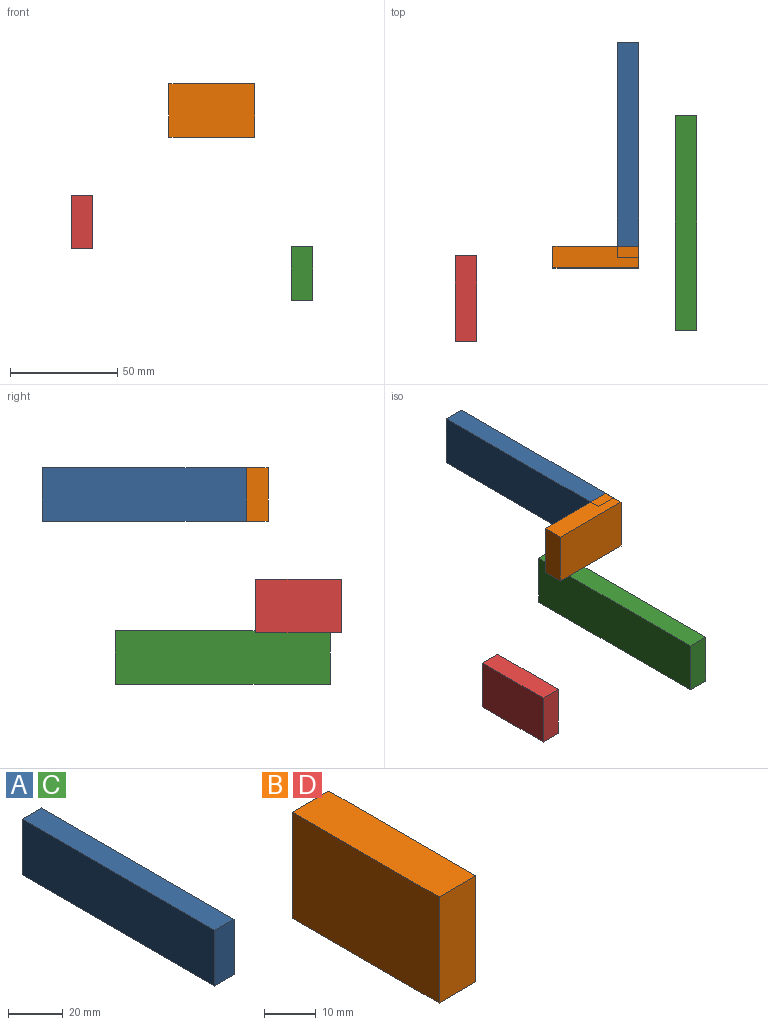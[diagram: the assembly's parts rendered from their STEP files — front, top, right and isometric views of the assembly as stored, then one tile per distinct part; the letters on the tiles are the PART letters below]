
ASSEMBLY  parts=4 mates=1
PART A: 6 faces, bbox 10x100x25 mm
  f0: plane 100x10mm, normal (0,0,1), area 1000mm2, adj f1,f3,f4,f5
  f1: plane 100x25mm, normal (-1,0,0), area 2500mm2, adj f0,f2,f4,f5
  f2: plane 100x10mm, normal (0,0,-1), area 1000mm2, adj f1,f3,f4,f5
  f3: plane 100x25mm, normal (1,0,0), area 2500mm2, adj f0,f2,f4,f5
  f4: plane 25x10mm, normal (0,-1,0), area 250mm2, adj f0,f1,f2,f3
  f5: plane 25x10mm, normal (0,1,0), area 250mm2, adj f0,f1,f2,f3
PART B: 6 faces, bbox 10x40x25 mm
  f0: plane 40x10mm, normal (0,0,1), area 400mm2, adj f1,f3,f4,f5
  f1: plane 40x25mm, normal (-1,0,0), area 1000mm2, adj f0,f2,f4,f5
  f2: plane 40x10mm, normal (0,0,-1), area 400mm2, adj f1,f3,f4,f5
  f3: plane 40x25mm, normal (1,0,0), area 1000mm2, adj f0,f2,f4,f5
  f4: plane 25x10mm, normal (0,-1,0), area 250mm2, adj f0,f1,f2,f3
  f5: plane 25x10mm, normal (0,1,0), area 250mm2, adj f0,f1,f2,f3
PART C: same geometry as A
PART D: same geometry as B
PLACE A t=(-29.79,-25.03,-30.45)mm
PLACE B rot(axis=(0,0,1),90deg) t=(-77.49,-126.33,-18.48)mm
PLACE C t=(-2.98,-59,-106.35)mm
PLACE D t=(-119.16,-124.25,-70.37)mm
MATE fastened B.f4 <-> A.f3  axis (1,0,0) through (-37.49,-125.03,-17.41)mm
